# Revit family: LLT-CM
name_source: partatom
category: Lighting Fixtures
revit_build: Autodesk Revit 2014 (Build: 20130308_1515(x64)
units: mm (PartAtom-declared; Revit-internal decimal feet)

## types (3) — shared parameters
Assembly Code = D5020200
Cable Height = 24"
Ceiling Type = Surface
Color Filter = 16777215
Color Temp = 3000K
Default Elevation = 48"
Description = LED Lensed Troffer with Advanced Solid State Technology
Dimming Lamp Color Temperature Shift = Incandescent Lamp Curve
Door = White Flush Aluminum
Emit Shape Visible in Rendering = No
Finish = Hubbell - Arctic White
Glass = Hubbell - White Glass
Lamp = LED
Load Classification = Lighting
Lumen Output = High Lumen
Manufacturer = Columbia Lighting
Model = LLT-CM
Photometric Link = https://www.hubbell.com
Photometric Web File = LLT24-30HLG-FSA12F-EDU.ies
Power Factor = 1
Product Documentation Link = https://hubbellcdn.com
Product Page URL = https://www.hubbell.com
Shielding = A12F Pattern 12 Frosted Acrylic Lens
Tilt Angle = 90.00°
Type Comments = Lighting Fixture
URL = https://www.hubbell.com
Voltage = 120 V
Warranty = Five year warranty

## per-type parameters (varying)
| type | Apparent Load | Emit from Rectangle Length | Emit from Rectangle Width | Wattage Comments | Watts | zz Length 1 | zz Length 2 |
| LLT14-CM | 36 VA | 46" | 10" | 22W, 27W, 36W,45W | 36 W | 12" | 48" |
| LLT22-CM | 36 VA | 22" | 22" | 22W, 27W, 36W,45W | 36 W | 24" | 24" |
| LLT24-CM | 45 VA | 46" | 22" | 33W, 38W, 45W,61W,75W | 45 W | 24" | 48" |

## geometry (parser evidence)
native form markers: Blend x3, Sweep x3
no freeform markers — native parametric forms only
